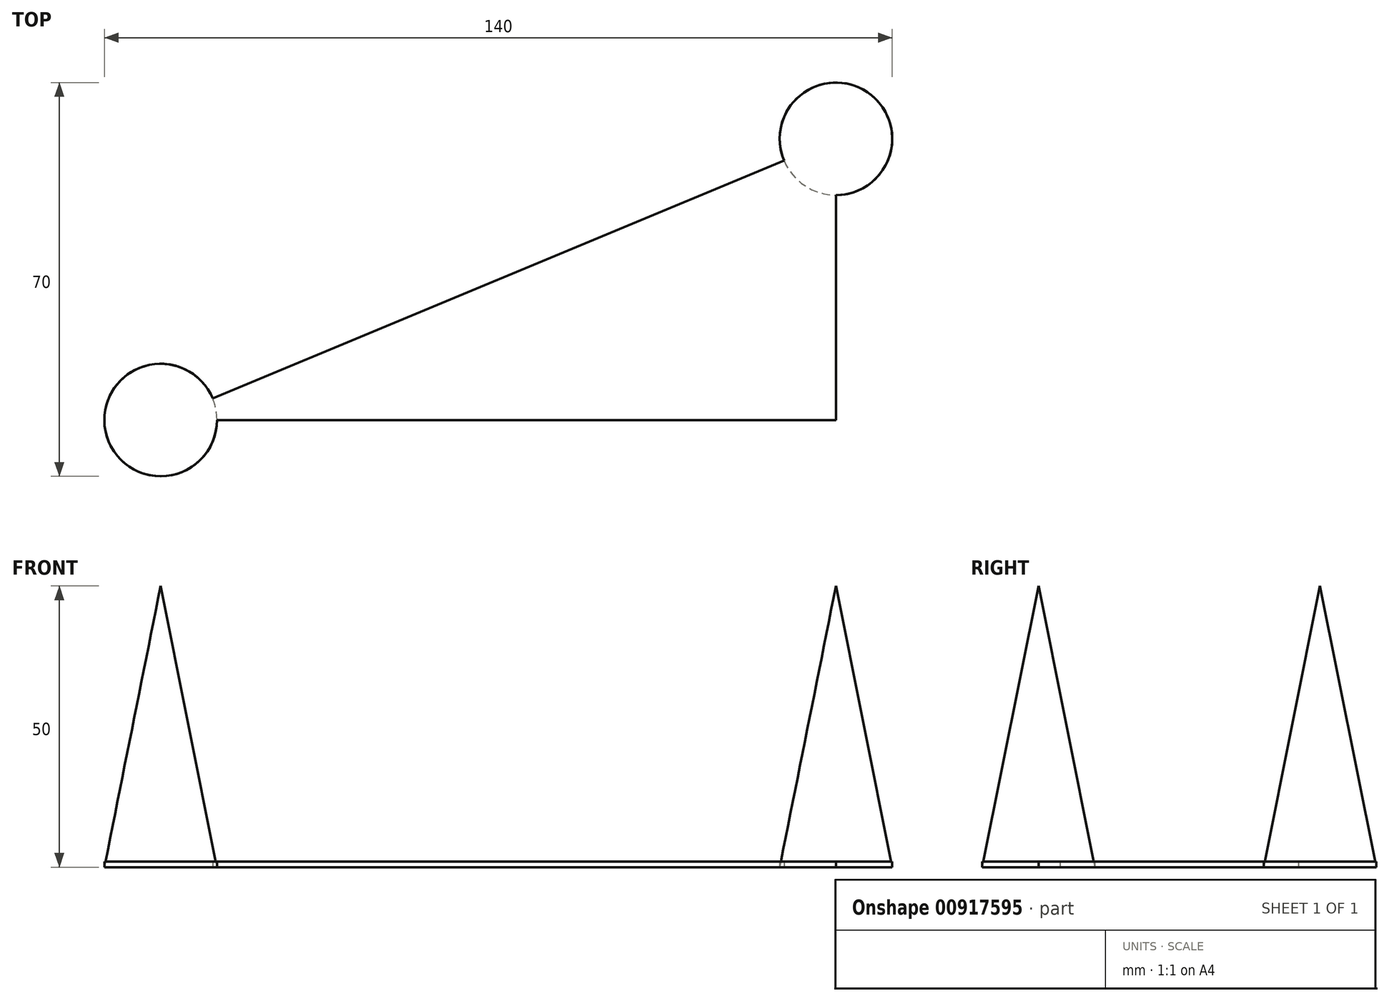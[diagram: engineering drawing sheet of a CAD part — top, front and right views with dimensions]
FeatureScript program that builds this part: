
annotation { "Feature Type Name" : "Feature", "Feature Type Description" : "" }
export const myFeature = defineFeature(function(context is Context, id is Id, definition is map)
    precondition{}
    {
        {
            var Q0;
            Q0=qCreatedBy(makeId("Top.planeOp"),FACE);
            var sketch = newSketch(context, id + "F0", { "sketchPlane" : qUnion([Q0])});
            skLineSegment(sketch, "E0", {"start": v(0, 0) * mm, "end": v(-120, 0) * mm});
            skLineSegment(sketch, "E1", {"start": v(0, 0) * mm, "end": v(0, 50) * mm});
            skCircle(sketch, "E2", {"center": v(-120, 0) * mm, "radius": 10 * mm});
            skCircle(sketch, "E3", {"center": v(0, 50) * mm, "radius": 10 * mm});
            skLineSegment(sketch, "E4", {"start": v(0, 50) * mm, "end": v(-120, 0) * mm});
            skSolve(sketch);
        }
        {
            var Q0;
            Q0=qCreatedBy(makeId("Front.planeOp"),FACE);
            var sketch = newSketch(context, id + "F1", { "sketchPlane" : qUnion([Q0])});
            skLineSegment(sketch, "E5", {"start": v(0, 0) * mm, "end": v(-120, 0) * mm});
            skLineSegment(sketch, "E6", {"start": v(-120, 0) * mm, "end": v(-120, 50) * mm});
            skLineSegment(sketch, "E7", {"start": v(-120, 0) * mm, "end": v(-130, 0) * mm});
            skLineSegment(sketch, "E8", {"start": v(-130, 0) * mm, "end": v(-120, 50) * mm});
            skSolve(sketch);
        }
        {
            var Q0;
            Q0=makeQuery(id+"F1.imprint","IMPRINT",FACE,{"disambiguationData":[TD([[makeQuery(id+"F1.imprint","IMPRINT",EDGE,{"derivedFrom":sQuery(id+"F1.wireOp",EDGE,"E6")}),1.0]])]});
            var Q1;
            Q1=sQuery(id+"F1.wireOp",EDGE,"E6");
            revolve(context, id + "F2", {"surfaceOperationType" : NewSurfaceOperationType.NEW, "entities" : qUnion([Q0]), "axis" : qUnion([Q1]), "revolveType" : RevolveType.FULL});
        }
        {
            var Q0;
            Q0=qCreatedBy(makeId("Front.planeOp"),FACE);
            cPlane(context, id + "F3", {"entities" : qUnion([Q0]), "cplaneType" : CPlaneType.OFFSET, "offset" : 50 * mm, "oppositeDirection" : true, "width" : 150 * mm, "height" : 150 * mm});
        }
        {
            var Q0;
            Q0=qCreatedBy(id+"F3.planeOp",FACE);
            var sketch = newSketch(context, id + "F4", { "sketchPlane" : qUnion([Q0])});
            skLineSegment(sketch, "E9", {"start": v(0, 0) * mm, "end": v(10, 0) * mm});
            skLineSegment(sketch, "E10", {"start": v(0, 0) * mm, "end": v(0, 50) * mm});
            skLineSegment(sketch, "E11", {"start": v(0, 50) * mm, "end": v(10, 0) * mm});
            skSolve(sketch);
        }
        {
            var Q0;
            Q0=makeQuery(id+"F4.imprint","IMPRINT",FACE,{"disambiguationData":[TD([[makeQuery(id+"F4.imprint","IMPRINT",EDGE,{"derivedFrom":sQuery(id+"F4.wireOp",EDGE,"E9")}),1.0]])]});
            var Q1;
            Q1=sQuery(id+"F4.wireOp",EDGE,"E10");
            revolve(context, id + "F5", {"surfaceOperationType" : NewSurfaceOperationType.NEW, "entities" : qUnion([Q0]), "axis" : qUnion([Q1]), "revolveType" : RevolveType.FULL});
        }
        {
            var Q0;
            {var subQ0=sQuery(id+"F0.wireOp",EDGE,"E4");var subQ1=sQuery(id+"F0.wireOp",EDGE,"E0");var subQ2=makeQuery(id+"F0.imprint","INTERSECT",VERTEX,{"derivedFrom":[subQ1,subQ0]});Q0=makeQuery(id+"F0.imprint","IMPRINT",FACE,{"disambiguationData":[TD([[makeQuery(id+"F0.imprint","IMPRINT",EDGE,{"disambiguationData":[TD([[subQ2,1.0]])],"derivedFrom":subQ1}),1.0]])]});}
            var Q1;
            {var subQ1=sQuery(id+"F0.wireOp",EDGE,"E1");var subQ6=sQuery(id+"F0.wireOp",EDGE,"E0");var subQ9=makeQuery(id+"F0.imprint","INTERSECT",VERTEX,{"derivedFrom":[subQ6,subQ1]});Q1=makeQuery(id+"F0.imprint","IMPRINT",FACE,{"disambiguationData":[TD([[makeQuery(id+"F0.imprint","IMPRINT",EDGE,{"disambiguationData":[TD([[subQ9,-1.0]])],"derivedFrom":subQ6}),-1.0]])]});}
            var Q2;
            {var subQ0=sQuery(id+"F0.wireOp",EDGE,"E4");var subQ1=sQuery(id+"F0.wireOp",EDGE,"E1");var subQ2=makeQuery(id+"F0.imprint","INTERSECT",VERTEX,{"derivedFrom":[subQ1,subQ0]});Q2=makeQuery(id+"F0.imprint","IMPRINT",FACE,{"disambiguationData":[TD([[makeQuery(id+"F0.imprint","IMPRINT",EDGE,{"disambiguationData":[TD([[subQ2,1.0]])],"derivedFrom":subQ1}),-1.0]])]});}
            var Q3;
            {var subQ0=sQuery(id+"F0.wireOp",EDGE,"E4");var subQ1=sQuery(id+"F0.wireOp",EDGE,"E0");var subQ2=makeQuery(id+"F0.imprint","INTERSECT",VERTEX,{"derivedFrom":[subQ1,subQ0]});Q3=makeQuery(id+"F0.imprint","IMPRINT",FACE,{"disambiguationData":[TD([[makeQuery(id+"F0.imprint","IMPRINT",EDGE,{"disambiguationData":[TD([[subQ2,1.0]])],"derivedFrom":subQ1}),-1.0]])]});}
            var Q4;
            {var subQ0=sQuery(id+"F0.wireOp",EDGE,"E4");var subQ1=sQuery(id+"F0.wireOp",EDGE,"E1");var subQ2=makeQuery(id+"F0.imprint","INTERSECT",VERTEX,{"derivedFrom":[subQ1,subQ0]});Q4=makeQuery(id+"F0.imprint","IMPRINT",FACE,{"disambiguationData":[TD([[makeQuery(id+"F0.imprint","IMPRINT",EDGE,{"disambiguationData":[TD([[subQ2,1.0]])],"derivedFrom":subQ1}),1.0]])]});}
            extrude(context, id + "F6", {"entities" : qUnion([Q0, Q1, Q2, Q3, Q4]), "depth" : 1 * mm, "offsetDistance" : 25 * mm});
        }
        {
            var Q0;
            Q0=makeQuery(id+"F6.opExtrude","SWEPT_FACE",FACE,{"disambiguationData":[OSD([sQuery(id+"F0.wireOp",EDGE,"E0")])]});
            cPlane(context, id + "F7", {"entities" : qUnion([Q0]), "cplaneType" : CPlaneType.OFFSET, "offset" : 25 * mm, "width" : 150 * mm, "height" : 150 * mm});
        }
    });
